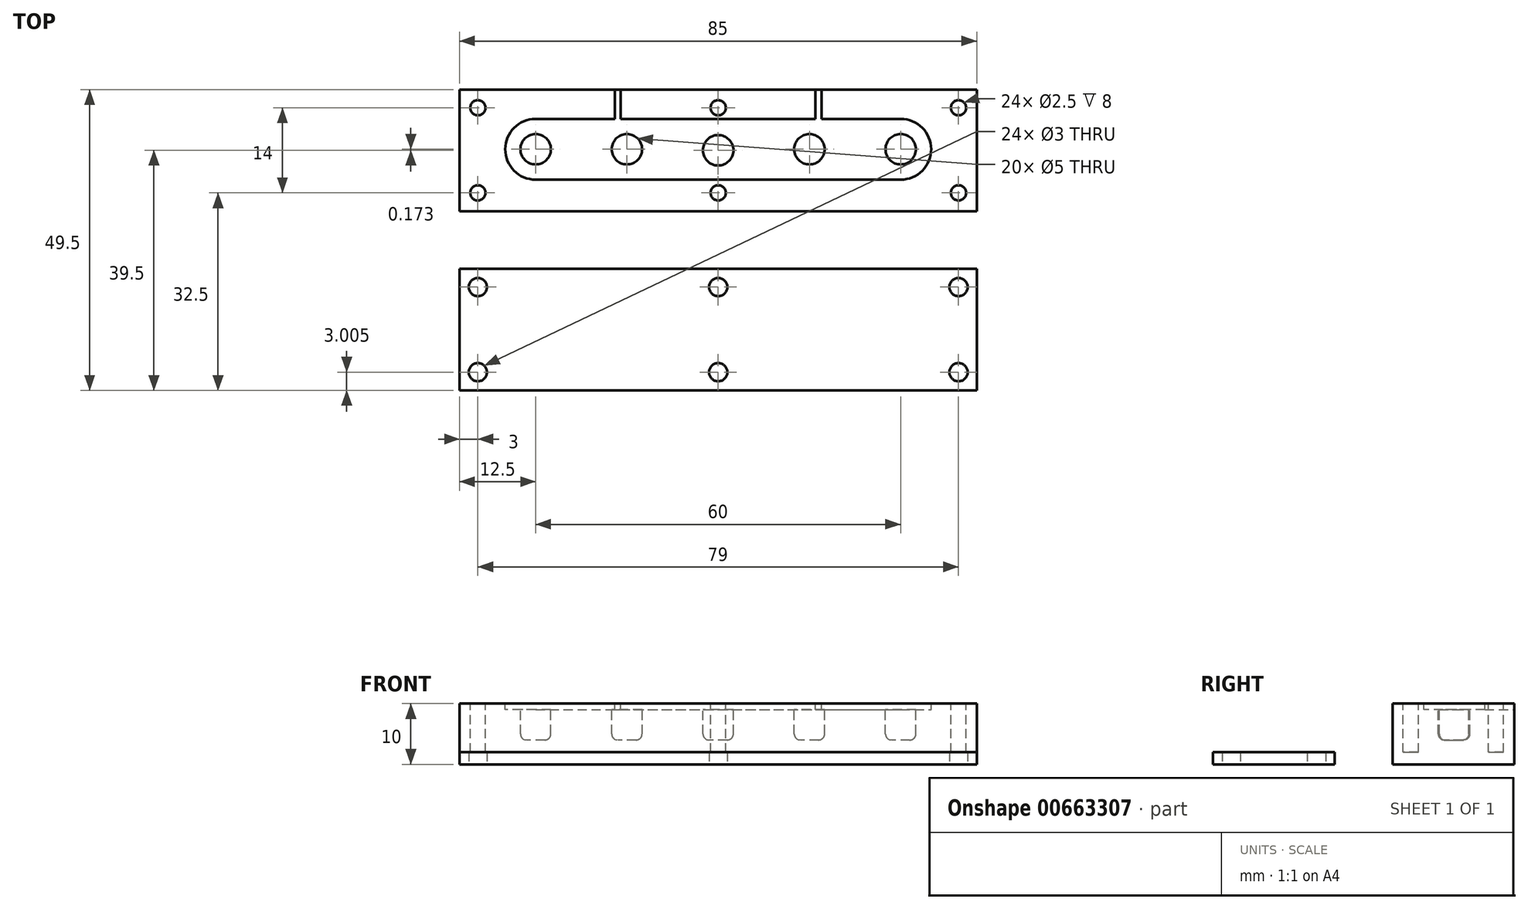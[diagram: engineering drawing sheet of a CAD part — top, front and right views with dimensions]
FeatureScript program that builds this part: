
annotation { "Feature Type Name" : "Feature", "Feature Type Description" : "" }
export const myFeature = defineFeature(function(context is Context, id is Id, definition is map)
    precondition{}
    {
        {
            var Q0;
            Q0=qCreatedBy(makeId("Top.planeOp"),FACE);
            var sketch = newSketch(context, id + "F0", { "sketchPlane" : qUnion([Q0])});
            skLineSegment(sketch, "E0.bottom", {"start": v(42.5, -10) * mm, "end": v(-42.5, -10) * mm});
            skLineSegment(sketch, "E0.top", {"start": v(42.5, 10) * mm, "end": v(-42.5, 10) * mm});
            skLineSegment(sketch, "E0.left", {"start": v(42.5, -10) * mm, "end": v(42.5, 10) * mm});
            skLineSegment(sketch, "E0.right", {"start": v(-42.5, -10) * mm, "end": v(-42.5, 10) * mm});
            skPoint(sketch, "E0.middle", {"position": v(0, 0) * mm});
            skSolve(sketch);
        }
        {
            var Q0;
            Q0=makeQuery(id+"F0.imprint","IMPRINT",FACE,{"disambiguationData":[TD([[makeQuery(id+"F0.imprint","IMPRINT",EDGE,{"derivedFrom":sQuery(id+"F0.wireOp",EDGE,"E0.bottom")}),-1.0]])]});
            extrude(context, id + "F1", {"entities" : qUnion([Q0]), "depth" : 10 * mm, "offsetDistance" : 25 * mm});
        }
        {
            var Q0;
            Q0=makeQuery(id+"F1.opExtrude","CAP_FACE",FACE,{"disambiguationData":[OSD([sQuery(id+"F0.wireOp",EDGE,"E0.bottom"),sQuery(id+"F0.wireOp",EDGE,"E0.top"),sQuery(id+"F0.wireOp",EDGE,"E0.left"),sQuery(id+"F0.wireOp",EDGE,"E0.right")])],"isStart":false});
            var sketch = newSketch(context, id + "F2", { "sketchPlane" : qUnion([Q0])});
            skArc(sketch, "E1", {"start": v(-30, 5.17) * mm, "mid": v(-35, 0.17) * mm, "end": v(-30, -4.83) * mm});
            skArc(sketch, "E2", {"start": v(30, -4.83) * mm, "mid": v(35, 0.17) * mm, "end": v(30, 5.17) * mm});
            skLineSegment(sketch, "E3", {"start": v(-30, -4.83) * mm, "end": v(30, -4.83) * mm});
            skLineSegment(sketch, "E4", {"start": v(-30, 5.17) * mm, "end": v(30, 5.17) * mm});
            skCircle(sketch, "E5", {"center": v(-30, 0.17) * mm, "radius": 2.5 * mm});
            skCircle(sketch, "E6", {"center": v(-15, 0.17) * mm, "radius": 2.5 * mm});
            skCircle(sketch, "E7", {"center": v(0, 0) * mm, "radius": 2.5 * mm});
            skCircle(sketch, "E8", {"center": v(15, 0.17) * mm, "radius": 2.5 * mm});
            skCircle(sketch, "E9", {"center": v(30, 0.17) * mm, "radius": 2.5 * mm});
            skSolve(sketch);
        }
        {
            var Q0;
            Q0=makeQuery(id+"F2.imprint","IMPRINT",FACE,{"disambiguationData":[TD([[makeQuery(id+"F2.imprint","IMPRINT",EDGE,{"derivedFrom":sQuery(id+"F2.wireOp",EDGE,"E5")}),1.0]])]});
            var Q1;
            Q1=makeQuery(id+"F2.imprint","IMPRINT",FACE,{"disambiguationData":[TD([[makeQuery(id+"F2.imprint","IMPRINT",EDGE,{"derivedFrom":sQuery(id+"F2.wireOp",EDGE,"E6")}),1.0]])]});
            var Q2;
            Q2=makeQuery(id+"F2.imprint","IMPRINT",FACE,{"disambiguationData":[TD([[makeQuery(id+"F2.imprint","IMPRINT",EDGE,{"derivedFrom":sQuery(id+"F2.wireOp",EDGE,"E7")}),1.0]])]});
            var Q3;
            Q3=makeQuery(id+"F2.imprint","IMPRINT",FACE,{"disambiguationData":[TD([[makeQuery(id+"F2.imprint","IMPRINT",EDGE,{"derivedFrom":sQuery(id+"F2.wireOp",EDGE,"E8")}),1.0]])]});
            var Q4;
            Q4=makeQuery(id+"F2.imprint","IMPRINT",FACE,{"disambiguationData":[TD([[makeQuery(id+"F2.imprint","IMPRINT",EDGE,{"derivedFrom":sQuery(id+"F2.wireOp",EDGE,"E9")}),1.0]])]});
            extrude(context, id + "F3", {"entities" : qUnion([Q0, Q1, Q2, Q3, Q4]), "operationType" : NewBodyOperationType.REMOVE, "oppositeDirection" : true, "depth" : 6 * mm, "offsetDistance" : 25 * mm});
        }
        {
            var Q0;
            Q0=makeQuery(id+"F2.imprint","IMPRINT",FACE,{"disambiguationData":[TD([[makeQuery(id+"F2.imprint","IMPRINT",EDGE,{"derivedFrom":sQuery(id+"F2.wireOp",EDGE,"E1")}),1.0]])]});
            extrude(context, id + "F4", {"entities" : qUnion([Q0]), "operationType" : NewBodyOperationType.REMOVE, "oppositeDirection" : true, "depth" : 1 * mm, "offsetDistance" : 25 * mm});
        }
        {
            var Q0;
            Q0=makeQuery(id+"F1.opExtrude","CAP_FACE",FACE,{"disambiguationData":[OSD([sQuery(id+"F0.wireOp",EDGE,"E0.bottom"),sQuery(id+"F0.wireOp",EDGE,"E0.top"),sQuery(id+"F0.wireOp",EDGE,"E0.left"),sQuery(id+"F0.wireOp",EDGE,"E0.right")])],"isStart":false});
            var sketch = newSketch(context, id + "F5", { "sketchPlane" : qUnion([Q0])});
            skCircle(sketch, "E10", {"center": v(-39.5, 7) * mm, "radius": 1.25 * mm});
            skCircle(sketch, "E11", {"center": v(-39.5, -7) * mm, "radius": 1.25 * mm});
            skCircle(sketch, "E12", {"center": v(39.5, -7) * mm, "radius": 1.25 * mm});
            skCircle(sketch, "E13", {"center": v(39.5, 7) * mm, "radius": 1.25 * mm});
            skLineSegment(sketch, "E14", {"start": v(-70.43, 7) * mm, "end": v(71.25, 7) * mm, "construction": true});
            skLineSegment(sketch, "E15", {"start": v(71.25, -7) * mm, "end": v(-70.69, -7) * mm, "construction": true});
            skLineSegment(sketch, "E16", {"start": v(39.5, 15.35) * mm, "end": v(39.5, -17.84) * mm, "construction": true});
            skLineSegment(sketch, "E17", {"start": v(-39.5, 16.03) * mm, "end": v(-39.5, -16.55) * mm, "construction": true});
            skLineSegment(sketch, "E18", {"start": v(0, 15.08) * mm, "end": v(0, -18.39) * mm, "construction": true});
            skCircle(sketch, "E19", {"center": v(0, 7) * mm, "radius": 1.25 * mm});
            skCircle(sketch, "E20", {"center": v(0, -7) * mm, "radius": 1.25 * mm});
            skSolve(sketch);
        }
        {
            var Q0;
            Q0=makeQuery(id+"F5.imprint","IMPRINT",FACE,{"disambiguationData":[TD([[makeQuery(id+"F5.imprint","IMPRINT",EDGE,{"derivedFrom":sQuery(id+"F5.wireOp",EDGE,"E10")}),1.0]])]});
            var Q1;
            Q1=makeQuery(id+"F5.imprint","IMPRINT",FACE,{"disambiguationData":[TD([[makeQuery(id+"F5.imprint","IMPRINT",EDGE,{"derivedFrom":sQuery(id+"F5.wireOp",EDGE,"E11")}),1.0]])]});
            var Q2;
            Q2=makeQuery(id+"F5.imprint","IMPRINT",FACE,{"disambiguationData":[TD([[makeQuery(id+"F5.imprint","IMPRINT",EDGE,{"derivedFrom":sQuery(id+"F5.wireOp",EDGE,"E13")}),1.0]])]});
            var Q3;
            Q3=makeQuery(id+"F5.imprint","IMPRINT",FACE,{"disambiguationData":[TD([[makeQuery(id+"F5.imprint","IMPRINT",EDGE,{"derivedFrom":sQuery(id+"F5.wireOp",EDGE,"E12")}),1.0]])]});
            var Q4;
            Q4=makeQuery(id+"F5.imprint","IMPRINT",FACE,{"disambiguationData":[TD([[makeQuery(id+"F5.imprint","IMPRINT",EDGE,{"derivedFrom":sQuery(id+"F5.wireOp",EDGE,"E19")}),1.0]])]});
            var Q5;
            Q5=makeQuery(id+"F5.imprint","IMPRINT",FACE,{"disambiguationData":[TD([[makeQuery(id+"F5.imprint","IMPRINT",EDGE,{"derivedFrom":sQuery(id+"F5.wireOp",EDGE,"E20")}),1.0]])]});
            extrude(context, id + "F6", {"entities" : qUnion([Q0, Q1, Q2, Q3, Q4, Q5]), "operationType" : NewBodyOperationType.REMOVE, "oppositeDirection" : true, "depth" : 8 * mm, "offsetDistance" : 25 * mm});
        }
        {
            var Q0;
            Q0=makeQuery(id+"F3.boolean.opBoolean","COPY",EDGE,{"derivedFrom":makeQuery(id+"F3.opExtrude","CAP_EDGE",EDGE,{"disambiguationData":[OSD([sQuery(id+"F2.wireOp",EDGE,"E5")])],"isStart":false})});
            var Q1;
            Q1=makeQuery(id+"F3.boolean.opBoolean","COPY",EDGE,{"derivedFrom":makeQuery(id+"F3.opExtrude","CAP_EDGE",EDGE,{"disambiguationData":[OSD([sQuery(id+"F2.wireOp",EDGE,"E6")])],"isStart":false})});
            var Q2;
            Q2=makeQuery(id+"F3.boolean.opBoolean","COPY",EDGE,{"derivedFrom":makeQuery(id+"F3.opExtrude","CAP_EDGE",EDGE,{"disambiguationData":[OSD([sQuery(id+"F2.wireOp",EDGE,"E7")])],"isStart":false})});
            var Q3;
            Q3=makeQuery(id+"F3.boolean.opBoolean","COPY",EDGE,{"derivedFrom":makeQuery(id+"F3.opExtrude","CAP_EDGE",EDGE,{"disambiguationData":[OSD([sQuery(id+"F2.wireOp",EDGE,"E8")])],"isStart":false})});
            var Q4;
            Q4=makeQuery(id+"F3.boolean.opBoolean","COPY",EDGE,{"derivedFrom":makeQuery(id+"F3.opExtrude","CAP_EDGE",EDGE,{"disambiguationData":[OSD([sQuery(id+"F2.wireOp",EDGE,"E9")])],"isStart":false})});
            fillet(context, id + "F7", {"entities" : qUnion([Q0, Q1, Q2, Q3, Q4]), "radius" : 1 * mm, "tangentPropagation" : true, "allowEdgeOverflow" : false});
        }
        {
            var Q0;
            Q0=makeQuery(id+"F1.opExtrude","CAP_FACE",FACE,{"disambiguationData":[OSD([sQuery(id+"F0.wireOp",EDGE,"E0.bottom"),sQuery(id+"F0.wireOp",EDGE,"E0.top"),sQuery(id+"F0.wireOp",EDGE,"E0.left"),sQuery(id+"F0.wireOp",EDGE,"E0.right")])],"isStart":false});
            var sketch = newSketch(context, id + "F8", { "sketchPlane" : qUnion([Q0])});
            skLineSegment(sketch, "E21.bottom", {"start": v(-17, 10) * mm, "end": v(-16, 10) * mm});
            skLineSegment(sketch, "E21.top", {"start": v(-17, 5.17) * mm, "end": v(-16, 5.17) * mm});
            skLineSegment(sketch, "E21.left", {"start": v(-17, 10) * mm, "end": v(-17, 5.17) * mm});
            skLineSegment(sketch, "E21.right", {"start": v(-16, 10) * mm, "end": v(-16, 5.17) * mm});
            skLineSegment(sketch, "E22.bottom", {"start": v(16, 10) * mm, "end": v(17, 10) * mm});
            skLineSegment(sketch, "E22.top", {"start": v(16, 5.17) * mm, "end": v(17, 5.17) * mm});
            skLineSegment(sketch, "E22.left", {"start": v(16, 10) * mm, "end": v(16, 5.17) * mm});
            skLineSegment(sketch, "E22.right", {"start": v(17, 10) * mm, "end": v(17, 5.17) * mm});
            skSolve(sketch);
        }
        {
            var Q0;
            Q0=makeQuery(id+"F8.imprint","IMPRINT",FACE,{"disambiguationData":[TD([[makeQuery(id+"F8.imprint","IMPRINT",EDGE,{"derivedFrom":sQuery(id+"F8.wireOp",EDGE,"E21.bottom")}),1.0]])]});
            var Q1;
            Q1=makeQuery(id+"F8.imprint","IMPRINT",FACE,{"disambiguationData":[TD([[makeQuery(id+"F8.imprint","IMPRINT",EDGE,{"derivedFrom":sQuery(id+"F8.wireOp",EDGE,"E22.bottom")}),1.0]])]});
            var Q2;
            Q2=makeQuery(id+"F4.boolean.opBoolean","COPY",FACE,{"derivedFrom":makeQuery(id+"F4.opExtrude","CAP_FACE",FACE,{"disambiguationData":[OSD([sQuery(id+"F2.wireOp",EDGE,"E1"),sQuery(id+"F2.wireOp",EDGE,"E2"),sQuery(id+"F2.wireOp",EDGE,"E3"),sQuery(id+"F2.wireOp",EDGE,"E4"),sQuery(id+"F2.wireOp",EDGE,"E5"),sQuery(id+"F2.wireOp",EDGE,"E6"),sQuery(id+"F2.wireOp",EDGE,"E7"),sQuery(id+"F2.wireOp",EDGE,"E8"),sQuery(id+"F2.wireOp",EDGE,"E9")])],"isStart":false})});
            extrude(context, id + "F9", {"entities" : qUnion([Q0, Q1]), "operationType" : NewBodyOperationType.REMOVE, "endBound" : BoundingType.UP_TO_SURFACE, "oppositeDirection" : true, "depth" : 25 * mm, "endBoundEntityFace" : qUnion([Q2]), "offsetDistance" : 25 * mm});
        }
        {
            var Q0;
            Q0=qCreatedBy(makeId("Top.planeOp"),FACE);
            var sketch = newSketch(context, id + "F10", { "sketchPlane" : qUnion([Q0])});
            skLineSegment(sketch, "E23.bottom", {"start": v(-42.5, -19.5) * mm, "end": v(42.5, -19.5) * mm});
            skLineSegment(sketch, "E23.top", {"start": v(-42.5, -39.5) * mm, "end": v(42.5, -39.5) * mm});
            skLineSegment(sketch, "E23.left", {"start": v(-42.5, -19.5) * mm, "end": v(-42.5, -39.5) * mm});
            skLineSegment(sketch, "E23.right", {"start": v(42.5, -19.5) * mm, "end": v(42.5, -39.5) * mm});
            skLineSegment(sketch, "E24.0", {"start": v(-42.5, -10) * mm, "end": v(-42.5, 10) * mm});
            skLineSegment(sketch, "E25.0", {"start": v(42.5, -10) * mm, "end": v(42.5, 10) * mm});
            skLineSegment(sketch, "E26", {"start": v(-42.5, -8.1) * mm, "end": v(-42.5, -58.07) * mm, "construction": true});
            skLineSegment(sketch, "E27", {"start": v(-52.95, -22.5) * mm, "end": v(61.76, -22.5) * mm, "construction": true});
            skLineSegment(sketch, "E28", {"start": v(61.34, -36.5) * mm, "end": v(-52.13, -36.5) * mm, "construction": true});
            skCircle(sketch, "E29", {"center": v(-39.5, -22.5) * mm, "radius": 1.5 * mm});
            skCircle(sketch, "E30", {"center": v(-39.5, -36.5) * mm, "radius": 1.5 * mm});
            skCircle(sketch, "E31", {"center": v(0, -22.5) * mm, "radius": 1.5 * mm});
            skCircle(sketch, "E32", {"center": v(0, -36.5) * mm, "radius": 1.5 * mm});
            skCircle(sketch, "E33", {"center": v(39.5, -22.5) * mm, "radius": 1.5 * mm});
            skCircle(sketch, "E34", {"center": v(39.5, -36.5) * mm, "radius": 1.5 * mm});
            skCircle(sketch, "E35.0", {"center": v(-39.5, -7) * mm, "radius": 1.25 * mm});
            skCircle(sketch, "E36.0", {"center": v(39.5, -7) * mm, "radius": 1.25 * mm});
            skSolve(sketch);
        }
        {
            var Q0;
            Q0=makeQuery(id+"F10.imprint","IMPRINT",FACE,{"disambiguationData":[TD([[makeQuery(id+"F10.imprint","IMPRINT",EDGE,{"derivedFrom":sQuery(id+"F10.wireOp",EDGE,"E23.bottom")}),-1.0]])]});
            extrude(context, id + "F11", {"entities" : qUnion([Q0]), "depth" : 2 * mm, "offsetDistance" : 25 * mm});
        }
    });
